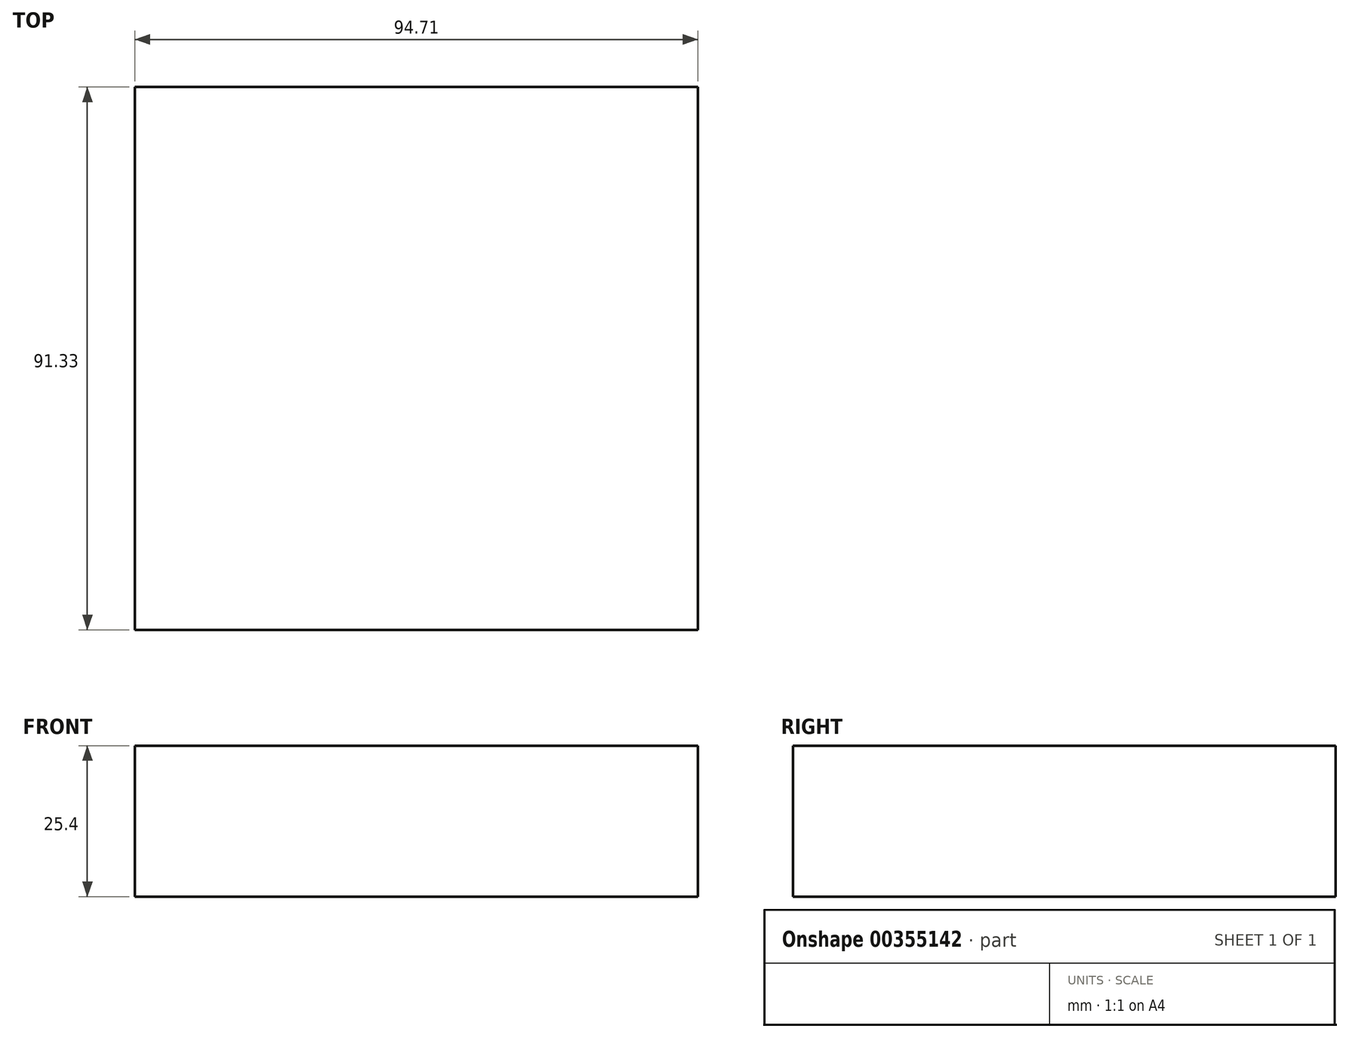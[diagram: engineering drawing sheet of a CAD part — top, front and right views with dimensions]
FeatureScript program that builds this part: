
annotation { "Feature Type Name" : "Feature", "Feature Type Description" : "" }
export const myFeature = defineFeature(function(context is Context, id is Id, definition is map)
    precondition{}
    {
        {
            var Q0;
            Q0=qCreatedBy(makeId("Top.planeOp"),FACE);
            var sketch = newSketch(context, id + "F0", { "sketchPlane" : qUnion([Q0])});
            skLineSegment(sketch, "E0.bottom", {"start": v(38.3, 45.2) * mm, "end": v(-56.41, 45.2) * mm});
            skLineSegment(sketch, "E0.top", {"start": v(38.3, -46.13) * mm, "end": v(-56.41, -46.13) * mm});
            skLineSegment(sketch, "E0.left", {"start": v(38.3, 45.2) * mm, "end": v(38.3, -46.13) * mm});
            skLineSegment(sketch, "E0.right", {"start": v(-56.41, 45.2) * mm, "end": v(-56.41, -46.13) * mm});
            skSolve(sketch);
        }
        {
            var Q0;
            Q0 = qSketchRegion(id + "F0", true);
            extrude(context, id + "F1", {"entities" : qUnion([Q0]), "depth" : 25.4 * mm});
        }
    });
